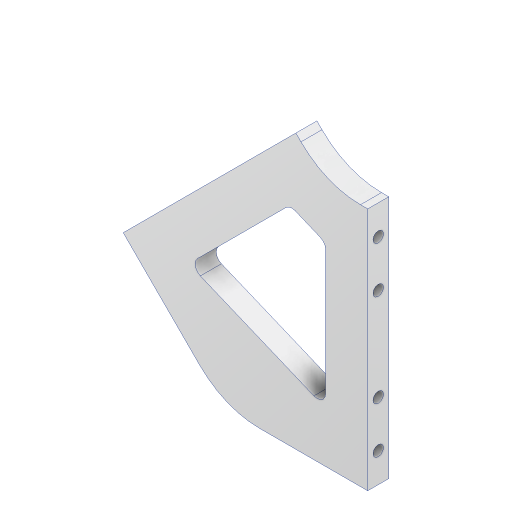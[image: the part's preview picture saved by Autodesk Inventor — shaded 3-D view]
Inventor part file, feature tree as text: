
AUTODESK INVENTOR PART (.ipt)
format: ipt  version: 2023.2 (Build 272271000, 271)  size: 202,752 bytes
history: native  units: mm
features: sketch x5, extrude x4, other x1, projected_geometry x1
ambient origin geometry x8: Origin, YZ Plane, XZ Plane, XY Plane, X Axis, Y Axis, Z Axis, Center Point
bodies: Body1 (feature_tree)
feature tree (11):
  other  "솔리드1"
  extrude  "돌출1"  Depth=58.0mm
  extrude  "돌출2"  Depth=10.0mm
  extrude  "돌출3"  Depth=10.0mm
  extrude  "돌출4"  TaperAngle=135.0deg  [1 undecoded]
  sketch  "스케치6"
  sketch  "스케치1"
  sketch  "스케치3"
  sketch  "스케치4"
  sketch  "스케치5"
  projected_geometry  "투영된 루프1"
note: 1 required parameter value undecoded (feature->parameter linkage not recoverable at this tier; creation-order binding heuristic only, values carry confidence <= 0.55)
